# Revit family: PRD_AR_PprTwlDspnsrs_STRATOSPaperTowelDispenser_STRX600E
name_source: partatom
category: Specialty Equipment
revit_build: Autodesk Revit 2018 (Build: 20190510_1515(x64)
units: mm (PartAtom-declared; Revit-internal decimal feet)

## family parameters
Cut with Voids When Loaded = Yes
Host = Face
OmniClass Number = 23.40.20.21.17
OmniClass Title = Paper Towel Dispensers, Disposal Units
Part Type = Normal
Room Calculation Point = No
Round Connector Dimension = Use Diameter
Shared = No

## types (1)
- STRX600E
    AssetType = Fixed
    BIMObjectName = PRD_AR_PaperTowelDispensers_STRATOSPaperTowelDispenser_STRX600E
    Category = Pr_40_70_22_62, Paper Towel Dispensers
    Default Elevation = 850 mm  [stored 2.78871 ft]
    Description = Paper towel dispenser for recessed mounting, stainless steel, surface satin finished, front with InoxPlus surface refinement for the reduction of finger marks and better cleaning characteristics (easy to clean), material thickness 1.5 mm, curved front cover, cylinder lock with KWC standard key, inspection window on front, loading capacity 300 - 400 pcs. of paper depending on convolution, includes stainless steel screws and dowels.
    DispenserMaterial = PRD_AR_StainlessSteel_SatinFinished
    DurationUnit = year
    Features = stainless steel, surface satin finished
    FillingQuantity = 400
    FillingQuantityUom = Towels
    Finish = satin finished
    GrossWeight = 8.10 kg
    IfcExportAs = IfcFurnitureType
    IfcExportType = USERDEFINED
    IntegralAccessories = incl. stainless steel screws and dowels
    IsBuiltIn = TRUE
    Lock = Key-lock
    MainColor = stainless steel
    Manufacturer = KWC Group AG
    ManufacturerName = KWC Group AG
    ManufacturerURL = www.kwc.com
    Material = stainless steel
    MaterialCode = 1.4301
    MaterialThickness = 1.50 mm
    Model = STRX600E
    ModelNumber = 2000057207
    ModelReference = STRX600E
    NBSDescription = Paper towel dispensers
    NBSReference = 45-35-72/344
    Name = Paper Towel Dispenser STRX600E
    NetWeight = 6.68 kg
    NominalDepth = 147 mm  [stored 0.482283 ft]
    NominalHeight = 632 mm
    NominalWidth = 327 mm
    Offset = 0 mm  [stored 0 ft]
    ProductInformation = https://pim.kwc.com
    Size = 327 x 632 x 147 mm
    Style = dispenser
    SurfaceTreatment = InoxPlus (anti fingerprint)
    TypeOfConsumable = Paper towel
    TypeOfFixing = Screw
    TypeOfMounting = Recessed mounting
    TypeOfOperation = Manual operation
    URL = www.kwc.com
    Uniclass2015Code = Pr_40_70_22_62
    Uniclass2015Title = Paper towel dispensers
    Uniclass2015Version = Products v1.10
    Version = 1
    WarrantyDurationUnit = year

note: [stored X ft] marks values corroborated as IEEE doubles in the binary element streams (Revit-internal decimal feet)

## geometry (parser evidence)
native form markers: Sweep x5
no freeform markers — native parametric forms only
